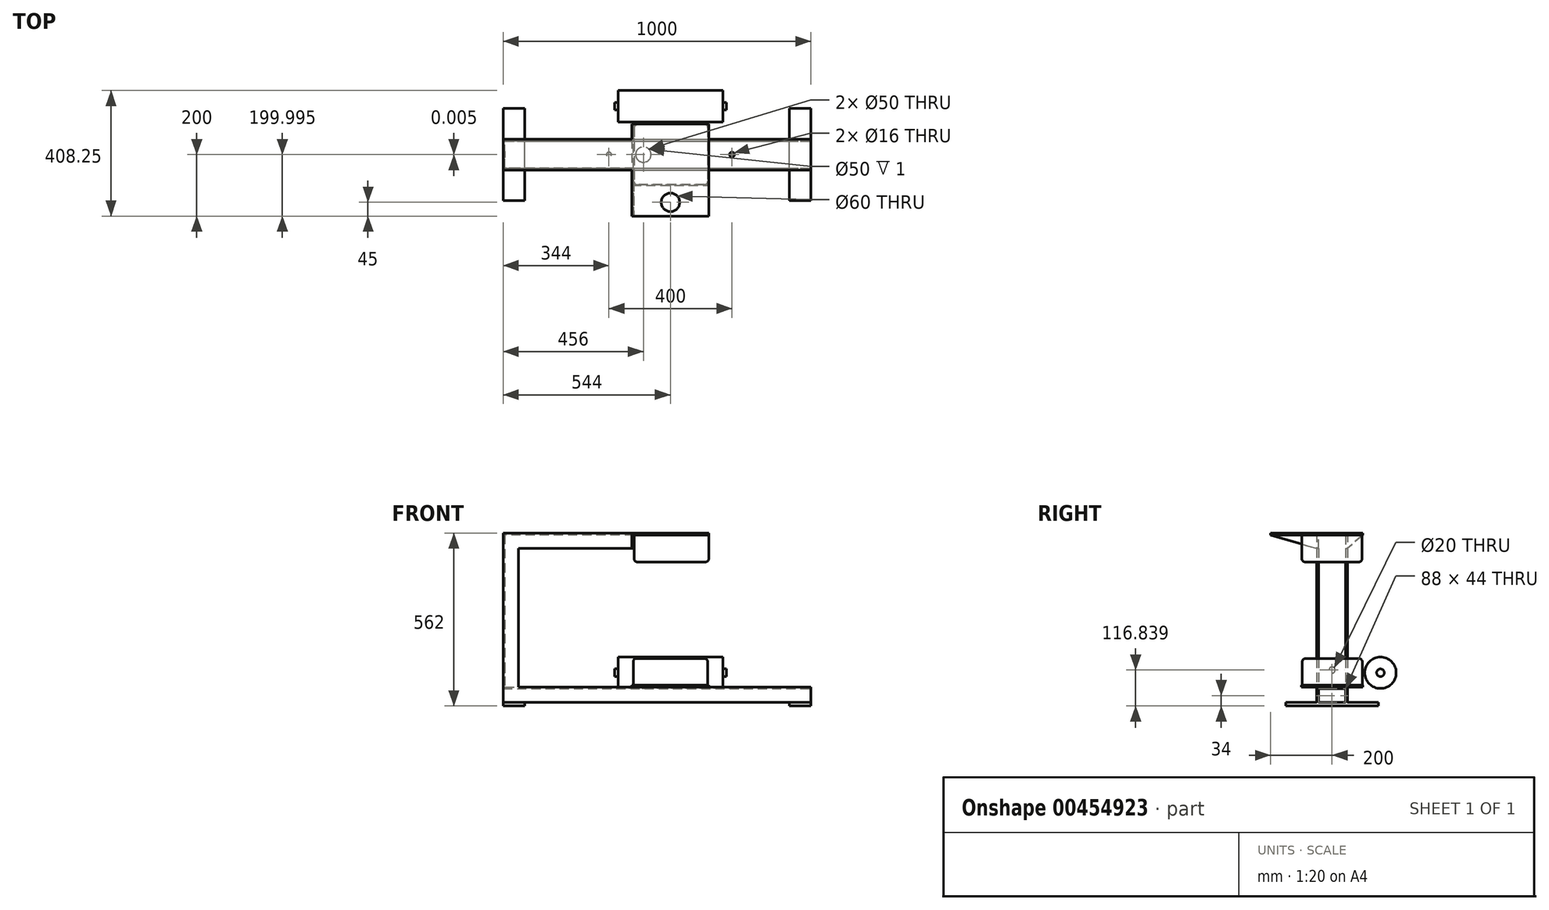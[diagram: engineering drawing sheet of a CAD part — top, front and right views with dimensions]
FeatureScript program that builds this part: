
annotation { "Feature Type Name" : "Feature", "Feature Type Description" : "" }
export const myFeature = defineFeature(function(context is Context, id is Id, definition is map)
    precondition{}
    {
        {
            var Q0;
            Q0=qCreatedBy(makeId("Right.planeOp"),FACE);
            var sketch = newSketch(context, id + "F0", { "sketchPlane" : qUnion([Q0])});
            skLineSegment(sketch, "E0", {"start": v(50, 0) * mm, "end": v(50, 50) * mm});
            skLineSegment(sketch, "E1", {"start": v(50, 50) * mm, "end": v(-50, 50) * mm});
            skLineSegment(sketch, "E2", {"start": v(-50, 50) * mm, "end": v(-50, 0) * mm});
            skLineSegment(sketch, "E3", {"start": v(-50, 0) * mm, "end": v(-44, 0) * mm});
            skLineSegment(sketch, "E4", {"start": v(-44, 0) * mm, "end": v(-44, 44) * mm});
            skLineSegment(sketch, "E5", {"start": v(-44, 44) * mm, "end": v(44, 44) * mm});
            skLineSegment(sketch, "E6", {"start": v(44, 44) * mm, "end": v(44, 0) * mm});
            skLineSegment(sketch, "E7", {"start": v(44, 0) * mm, "end": v(50, 0) * mm});
            skSolve(sketch);
        }
        {
            var Q0;
            Q0=qSketchRegion(id+"F0",true);
            extrude(context, id + "F1", {"entities" : qUnion([Q0]), "oppositeDirection" : true, "depth" : 1000 * mm});
        }
        {
            var Q0;
            Q0=makeQuery(id+"F1.opExtrude","SWEPT_FACE",FACE,{"disambiguationData":[OSD([sQuery(id+"F0.wireOp",EDGE,"E1")])]});
            var sketch = newSketch(context, id + "F2", { "sketchPlane" : qUnion([Q0])});
            skLineSegment(sketch, "E8", {"start": v(-1000, 50) * mm, "end": v(-1000, -50) * mm});
            skLineSegment(sketch, "E9", {"start": v(-1000, -50) * mm, "end": v(-950, -50) * mm});
            skLineSegment(sketch, "E10", {"start": v(-950, -50) * mm, "end": v(-950, -44) * mm});
            skLineSegment(sketch, "E11", {"start": v(-950, -44) * mm, "end": v(-994, -44) * mm});
            skLineSegment(sketch, "E12", {"start": v(-994, -44) * mm, "end": v(-994, 44) * mm});
            skLineSegment(sketch, "E13", {"start": v(-994, 44) * mm, "end": v(-950, 44) * mm});
            skLineSegment(sketch, "E14", {"start": v(-950, 44) * mm, "end": v(-950, 50) * mm});
            skLineSegment(sketch, "E15", {"start": v(-950, 50) * mm, "end": v(-1000, 50) * mm});
            skSolve(sketch);
        }
        {
            var Q0;
            Q0=makeQuery(id+"F2.imprint","IMPRINT",FACE,{"disambiguationData":[TD([[makeQuery(id+"F2.imprint","IMPRINT",EDGE,{"derivedFrom":sQuery(id+"F2.wireOp",EDGE,"E8")}),1.0]])]});
            extrude(context, id + "F3", {"entities" : qUnion([Q0]), "operationType" : NewBodyOperationType.ADD, "depth" : 500 * mm});
        }
        {
            var Q0;
            Q0=makeQuery(id+"F3.opExtrude","SWEPT_FACE",FACE,{"disambiguationData":[OSD([sQuery(id+"F2.wireOp",EDGE,"E14")])]});
            var sketch = newSketch(context, id + "F4", { "sketchPlane" : qUnion([Q0])});
            skLineSegment(sketch, "E16", {"start": v(50, 550) * mm, "end": v(-50, 550) * mm});
            skLineSegment(sketch, "E17", {"start": v(-50, 550) * mm, "end": v(-50, 500) * mm});
            skLineSegment(sketch, "E18", {"start": v(-50, 500) * mm, "end": v(-44, 500) * mm});
            skLineSegment(sketch, "E19", {"start": v(-44, 500) * mm, "end": v(-44, 544) * mm});
            skLineSegment(sketch, "E20", {"start": v(-44, 544) * mm, "end": v(44, 544) * mm});
            skLineSegment(sketch, "E21", {"start": v(44, 544) * mm, "end": v(44, 500) * mm});
            skLineSegment(sketch, "E22", {"start": v(44, 500) * mm, "end": v(50, 500) * mm});
            skLineSegment(sketch, "E23", {"start": v(50, 500) * mm, "end": v(50, 550) * mm});
            skSolve(sketch);
        }
        {
            var Q0;
            Q0=qSketchRegion(id+"F4",true);
            extrude(context, id + "F5", {"entities" : qUnion([Q0]), "operationType" : NewBodyOperationType.ADD, "depth" : 369 * mm, "hasSecondDirection" : true, "secondDirectionOppositeDirection" : true, "secondDirectionDepth" : 50 * mm});
        }
        {
            var Q0;
            Q0=makeQuery(id+"F5.opExtrude","CAP_FACE",FACE,{"disambiguationData":[OSD([sQuery(id+"F4.wireOp",EDGE,"E16"),sQuery(id+"F4.wireOp",EDGE,"E17"),sQuery(id+"F4.wireOp",EDGE,"E18"),sQuery(id+"F4.wireOp",EDGE,"E19"),sQuery(id+"F4.wireOp",EDGE,"E20"),sQuery(id+"F4.wireOp",EDGE,"E21"),sQuery(id+"F4.wireOp",EDGE,"E22"),sQuery(id+"F4.wireOp",EDGE,"E23")])],"isStart":false});
            var sketch = newSketch(context, id + "F6", { "sketchPlane" : qUnion([Q0])});
            skLineSegment(sketch, "E24", {"start": v(0, 550) * mm, "end": v(100, 550) * mm});
            skLineSegment(sketch, "E25", {"start": v(100, 550) * mm, "end": v(100, 544) * mm});
            skLineSegment(sketch, "E26", {"start": v(100, 544) * mm, "end": v(-200, 544) * mm});
            skLineSegment(sketch, "E27", {"start": v(-200, 544) * mm, "end": v(-200, 550) * mm});
            skLineSegment(sketch, "E28", {"start": v(-200, 550) * mm, "end": v(0, 550) * mm});
            skSolve(sketch);
        }
        {
            var Q0;
            Q0=qSketchRegion(id+"F6",true);
            extrude(context, id + "F7", {"entities" : qUnion([Q0]), "operationType" : NewBodyOperationType.ADD, "depth" : 250 * mm});
        }
        {
            var Q0;
            {var subQ0=sQuery(id+"F4.wireOp",EDGE,"E17");var subQ2=sQuery(id+"F4.wireOp",EDGE,"E18");var subQ3=sQuery(id+"F4.wireOp",EDGE,"E19");var subQ4=sQuery(id+"F4.wireOp",EDGE,"E20");Q0=makeQuery(id+"F7.boolean.opBoolean","SPLIT",FACE,{"disambiguationData":[TD([makeQuery(id+"F1.opExtrude","SWEPT_FACE",FACE,{"disambiguationData":[OSD([sQuery(id+"F0.wireOp",EDGE,"E2")])]})])],"derivedFrom":makeQuery(id+"F5.opExtrude","CAP_FACE",FACE,{"disambiguationData":[OSD([sQuery(id+"F4.wireOp",EDGE,"E16"),subQ0,subQ2,subQ3,subQ4,sQuery(id+"F4.wireOp",EDGE,"E21"),sQuery(id+"F4.wireOp",EDGE,"E22"),sQuery(id+"F4.wireOp",EDGE,"E23")])],"isStart":false})});}
            var sketch = newSketch(context, id + "F8", { "sketchPlane" : qUnion([Q0])});
            skLineSegment(sketch, "E29", {"start": v(-44, 544) * mm, "end": v(-200, 544) * mm});
            skLineSegment(sketch, "E30", {"start": v(-200, 544) * mm, "end": v(-50, 500) * mm});
            skLineSegment(sketch, "E31", {"start": v(-50, 500) * mm, "end": v(-44, 500) * mm});
            skLineSegment(sketch, "E32", {"start": v(-44, 544) * mm, "end": v(-44, 500) * mm});
            skSolve(sketch);
        }
        {
            var Q0;
            Q0=qSketchRegion(id+"F8",true);
            extrude(context, id + "F9", {"entities" : qUnion([Q0]), "operationType" : NewBodyOperationType.ADD, "depth" : 6 * mm});
        }
        {
            var Q0;
            {var subQ0=sQuery(id+"F4.wireOp",EDGE,"E20");var subQ2=sQuery(id+"F4.wireOp",EDGE,"E21");var subQ3=sQuery(id+"F4.wireOp",EDGE,"E22");var subQ4=sQuery(id+"F4.wireOp",EDGE,"E23");Q0=makeQuery(id+"F7.boolean.opBoolean","SPLIT",FACE,{"disambiguationData":[TD([makeQuery(id+"F1.opExtrude","SWEPT_FACE",FACE,{"disambiguationData":[OSD([sQuery(id+"F0.wireOp",EDGE,"E0")])]})])],"derivedFrom":makeQuery(id+"F5.opExtrude","CAP_FACE",FACE,{"disambiguationData":[OSD([sQuery(id+"F4.wireOp",EDGE,"E16"),sQuery(id+"F4.wireOp",EDGE,"E17"),sQuery(id+"F4.wireOp",EDGE,"E18"),sQuery(id+"F4.wireOp",EDGE,"E19"),subQ0,subQ2,subQ3,subQ4])],"isStart":false})});}
            var sketch = newSketch(context, id + "F10", { "sketchPlane" : qUnion([Q0])});
            skLineSegment(sketch, "E33", {"start": v(44, 544) * mm, "end": v(100, 544) * mm});
            skLineSegment(sketch, "E34", {"start": v(100, 544) * mm, "end": v(50, 500) * mm});
            skLineSegment(sketch, "E35", {"start": v(50, 500) * mm, "end": v(44, 500) * mm});
            skLineSegment(sketch, "E36", {"start": v(44, 500) * mm, "end": v(44, 544) * mm});
            skSolve(sketch);
        }
        {
            var Q0;
            Q0=qSketchRegion(id+"F10",true);
            extrude(context, id + "F11", {"entities" : qUnion([Q0]), "operationType" : NewBodyOperationType.ADD, "depth" : 6 * mm});
        }
        {
            var Q0;
            Q0=makeQuery(id+"F3.boolean.opBoolean","MERGE",FACE,{"derivedFrom":[makeQuery(id+"F1.opExtrude","CAP_FACE",FACE,{"disambiguationData":[OSD([sQuery(id+"F0.wireOp",EDGE,"E0"),sQuery(id+"F0.wireOp",EDGE,"E1"),sQuery(id+"F0.wireOp",EDGE,"E2"),sQuery(id+"F0.wireOp",EDGE,"E3"),sQuery(id+"F0.wireOp",EDGE,"E4"),sQuery(id+"F0.wireOp",EDGE,"E5"),sQuery(id+"F0.wireOp",EDGE,"E6"),sQuery(id+"F0.wireOp",EDGE,"E7")])],"isStart":false}),makeQuery(id+"F3.opExtrude","SWEPT_FACE",FACE,{"disambiguationData":[OSD([sQuery(id+"F2.wireOp",EDGE,"E8")])]})]});
            var sketch = newSketch(context, id + "F12", { "sketchPlane" : qUnion([Q0])});
            skCircle(sketch, "E37", {"center": v(0, 104.84) * mm, "radius": 10 * mm});
            skSolve(sketch);
        }
        {
            var Q0;
            Q0=makeQuery(id+"F12.imprint","IMPRINT",FACE,{"disambiguationData":[TD([[makeQuery(id+"F12.imprint","IMPRINT",EDGE,{"derivedFrom":sQuery(id+"F12.wireOp",EDGE,"E37")}),1.0]])]});
            extrude(context, id + "F13", {"entities" : qUnion([Q0]), "operationType" : NewBodyOperationType.REMOVE, "endBound" : BoundingType.THROUGH_ALL, "oppositeDirection" : true, "depth" : 25 * mm});
        }
        {
            var Q0;
            Q0=makeQuery(id+"F1.opExtrude","SWEPT_FACE",FACE,{"disambiguationData":[OSD([sQuery(id+"F0.wireOp",EDGE,"E1")])]});
            var sketch = newSketch(context, id + "F14", { "sketchPlane" : qUnion([Q0])});
            skCircle(sketch, "E38", {"center": v(-544, 0) * mm, "radius": 25 * mm});
            skLineSegment(sketch, "E39", {"start": v(-994, 0) * mm, "end": v(-544, 0) * mm});
            skSolve(sketch);
        }
        {
            var Q0;
            Q0=makeQuery(id+"F14.imprint","IMPRINT",FACE,{"disambiguationData":[TD([[makeQuery(id+"F14.imprint","IMPRINT",EDGE,{"derivedFrom":sQuery(id+"F14.wireOp",EDGE,"E38")}),1.0]])]});
            extrude(context, id + "F15", {"entities" : qUnion([Q0]), "operationType" : NewBodyOperationType.REMOVE, "oppositeDirection" : true, "depth" : 6 * mm});
        }
        {
            var Q0;
            Q0=makeQuery(id+"F7.boolean.opBoolean","MERGE",FACE,{"derivedFrom":[makeQuery(id+"F5.boolean.opBoolean","MERGE",FACE,{"derivedFrom":[makeQuery(id+"F3.opExtrude","CAP_FACE",FACE,{"disambiguationData":[OSD([sQuery(id+"F2.wireOp",EDGE,"E8"),sQuery(id+"F2.wireOp",EDGE,"E9"),sQuery(id+"F2.wireOp",EDGE,"E10"),sQuery(id+"F2.wireOp",EDGE,"E11"),sQuery(id+"F2.wireOp",EDGE,"E12"),sQuery(id+"F2.wireOp",EDGE,"E13"),sQuery(id+"F2.wireOp",EDGE,"E14"),sQuery(id+"F2.wireOp",EDGE,"E15")])],"isStart":false}),makeQuery(id+"F5.opExtrude","SWEPT_FACE",FACE,{"disambiguationData":[OSD([sQuery(id+"F4.wireOp",EDGE,"E16")])]})]}),makeQuery(id+"F7.opExtrude","SWEPT_FACE",FACE,{"disambiguationData":[OSD([sQuery(id+"F6.wireOp",EDGE,"E24"),sQuery(id+"F6.wireOp",EDGE,"E28")])]})]});
            var sketch = newSketch(context, id + "F16", { "sketchPlane" : qUnion([Q0])});
            skCircle(sketch, "E40", {"center": v(-456, -155) * mm, "radius": 30 * mm});
            skLineSegment(sketch, "E41", {"start": v(-456, -200) * mm, "end": v(-456, -155) * mm});
            skSolve(sketch);
        }
        {
            var Q0;
            Q0=makeQuery(id+"F16.imprint","IMPRINT",FACE,{"disambiguationData":[TD([[makeQuery(id+"F16.imprint","IMPRINT",EDGE,{"derivedFrom":sQuery(id+"F16.wireOp",EDGE,"E40")}),1.0]])]});
            extrude(context, id + "F17", {"entities" : qUnion([Q0]), "operationType" : NewBodyOperationType.REMOVE, "endBound" : BoundingType.THROUGH_ALL, "oppositeDirection" : true, "depth" : 25 * mm});
        }
        {
            var Q0;
            Q0=makeQuery(id+"F1.opExtrude","SWEPT_FACE",FACE,{"disambiguationData":[OSD([sQuery(id+"F0.wireOp",EDGE,"E1")])]});
            var sketch = newSketch(context, id + "F18", { "sketchPlane" : qUnion([Q0])});
            skLineSegment(sketch, "E42", {"start": v(-556, 100) * mm, "end": v(-556, 50) * mm});
            skLineSegment(sketch, "E43", {"start": v(-331, -100.18) * mm, "end": v(-331, 99.82) * mm});
            skLineSegment(sketch, "E44", {"start": v(-331, 99.82) * mm, "end": v(-581, 99.82) * mm});
            skLineSegment(sketch, "E45", {"start": v(-581, 99.82) * mm, "end": v(-581, -100.18) * mm});
            skLineSegment(sketch, "E46", {"start": v(-581, -100.18) * mm, "end": v(-331, -100.18) * mm});
            skLineSegment(sketch, "E47", {"start": v(-950, -50) * mm, "end": v(-581, -50) * mm});
            skSolve(sketch);
        }
        {
            var Q0;
            Q0=qSketchRegion(id+"F18",true);
            extrude(context, id + "F19", {"entities" : qUnion([Q0]), "operationType" : NewBodyOperationType.ADD, "depth" : 6 * mm});
        }
        {
            var Q0;
            Q0=makeQuery(id+"F1.opExtrude","SWEPT_FACE",FACE,{"disambiguationData":[OSD([sQuery(id+"F0.wireOp",EDGE,"E3")])]});
            var sketch = newSketch(context, id + "F20", { "sketchPlane" : qUnion([Q0])});
            skLineSegment(sketch, "E48", {"start": v(-1000, 50) * mm, "end": v(-1000, 150) * mm});
            skLineSegment(sketch, "E49", {"start": v(-1000, 150) * mm, "end": v(-930, 150) * mm});
            skLineSegment(sketch, "E50", {"start": v(-930, 150) * mm, "end": v(-930, -150) * mm});
            skLineSegment(sketch, "E51", {"start": v(-930, -150) * mm, "end": v(-1000, -150) * mm});
            skLineSegment(sketch, "E52", {"start": v(-1000, -150) * mm, "end": v(-1000, 50) * mm});
            skLineSegment(sketch, "E53", {"start": v(0, 50) * mm, "end": v(0, 150) * mm});
            skLineSegment(sketch, "E54", {"start": v(0, 150) * mm, "end": v(-70, 150) * mm});
            skLineSegment(sketch, "E55", {"start": v(-70, 150) * mm, "end": v(-70, -150) * mm});
            skLineSegment(sketch, "E56", {"start": v(-70, -150) * mm, "end": v(0, -150) * mm});
            skLineSegment(sketch, "E57", {"start": v(0, -150) * mm, "end": v(0, 50) * mm});
            skSolve(sketch);
        }
        {
            var Q0;
            Q0=qSketchRegion(id+"F20",true);
            extrude(context, id + "F21", {"entities" : qUnion([Q0]), "operationType" : NewBodyOperationType.ADD, "depth" : 12 * mm});
        }
        {
            var Q0;
            Q0=makeQuery(id+"F19.boolean.opBoolean","SPLIT",FACE,{"disambiguationData":[TD([makeQuery(id+"F3.opExtrude","SWEPT_FACE",FACE,{"disambiguationData":[OSD([sQuery(id+"F2.wireOp",EDGE,"E10")])]})])],"derivedFrom":makeQuery(id+"F1.opExtrude","SWEPT_FACE",FACE,{"disambiguationData":[OSD([sQuery(id+"F0.wireOp",EDGE,"E1")])]})});
            var sketch = newSketch(context, id + "F22", { "sketchPlane" : qUnion([Q0])});
            skPoint(sketch, "E58.endSnap0", {"position": v(-994, 0) * mm});
            skLineSegment(sketch, "E59", {"start": v(0, 0) * mm, "end": v(-256, 0) * mm});
            skLineSegment(sketch, "E60", {"start": v(-256, 0) * mm, "end": v(-656, 0) * mm});
            skPoint(sketch, "E60.endSnap0", {"position": v(-581, 0) * mm});
            skCircle(sketch, "E61", {"center": v(-656, 0) * mm, "radius": 8 * mm});
            skCircle(sketch, "E62", {"center": v(-256, 0) * mm, "radius": 8 * mm});
            skSolve(sketch);
        }
        {
            var Q0;
            Q0=qSketchRegion(id+"F22",true);
            extrude(context, id + "F23", {"entities" : qUnion([Q0]), "operationType" : NewBodyOperationType.REMOVE, "oppositeDirection" : true, "depth" : 6 * mm});
        }
        {
            var Q0;
            Q0=qCreatedBy(makeId("Top.planeOp"),FACE);
            var sketch = newSketch(context, id + "F24", { "sketchPlane" : qUnion([Q0])});
            skLineSegment(sketch, "E63", {"start": v(93.08, 453.86) * mm, "end": v(288.08, 453.86) * mm});
            skLineSegment(sketch, "E64", {"start": v(288.08, 453.86) * mm, "end": v(288.08, 211.86) * mm});
            skLineSegment(sketch, "E65", {"start": v(288.08, 211.86) * mm, "end": v(93.08, 211.86) * mm});
            skLineSegment(sketch, "E66", {"start": v(93.08, 211.86) * mm, "end": v(93.08, 453.86) * mm});
            skSolve(sketch);
        }
        {
            var Q0;
            Q0=qSketchRegion(id+"F24",true);
            extrude(context, id + "F25", {"entities" : qUnion([Q0]), "depth" : 87 * mm});
        }
        {
            var Q0;
            Q0=makeQuery(id+"F25.opExtrude","CAP_EDGE",EDGE,{"disambiguationData":[OSD([sQuery(id+"F24.wireOp",EDGE,"E64")])],"isStart":false});
            var Q1;
            Q1=makeQuery(id+"F25.opExtrude","CAP_EDGE",EDGE,{"disambiguationData":[OSD([sQuery(id+"F24.wireOp",EDGE,"E66")])],"isStart":false});
            var Q2;
            Q2=makeQuery(id+"F25.opExtrude","CAP_EDGE",EDGE,{"disambiguationData":[OSD([sQuery(id+"F24.wireOp",EDGE,"E65")])],"isStart":false});
            var Q3;
            Q3=makeQuery(id+"F25.opExtrude","CAP_EDGE",EDGE,{"disambiguationData":[OSD([sQuery(id+"F24.wireOp",EDGE,"E63")])],"isStart":false});
            var Q4;
            Q4=makeQuery(id+"F25.opExtrude","SWEPT_EDGE",EDGE,{"disambiguationData":[OSD([sQuery(id+"F24.wireOp",EDGE,"E63"),sQuery(id+"F24.wireOp",EDGE,"E64")])]});
            var Q5;
            Q5=makeQuery(id+"F25.opExtrude","SWEPT_EDGE",EDGE,{"disambiguationData":[OSD([sQuery(id+"F24.wireOp",EDGE,"E64"),sQuery(id+"F24.wireOp",EDGE,"E65")])]});
            var Q6;
            Q6=makeQuery(id+"F25.opExtrude","SWEPT_EDGE",EDGE,{"disambiguationData":[OSD([sQuery(id+"F24.wireOp",EDGE,"E65"),sQuery(id+"F24.wireOp",EDGE,"E66")])]});
            var Q7;
            Q7=makeQuery(id+"F25.opExtrude","SWEPT_EDGE",EDGE,{"disambiguationData":[OSD([sQuery(id+"F24.wireOp",EDGE,"E63"),sQuery(id+"F24.wireOp",EDGE,"E66")])]});
            fillet(context, id + "F26", {"entities" : qUnion([Q0, Q1, Q2, Q3, Q4, Q5, Q6, Q7]), "radius" : 10 * mm, "tangentPropagation" : true, "allowEdgeOverflow" : false});
        }
        {
            var Q0;
            Q0=makeQuery(id+"F25.opExtrude","SWEPT_BODY",BODY,{"disambiguationData":[OSD([sQuery(id+"F24.wireOp",EDGE,"E63"),sQuery(id+"F24.wireOp",EDGE,"E64"),sQuery(id+"F24.wireOp",EDGE,"E65"),sQuery(id+"F24.wireOp",EDGE,"E66")])]});
            transform(context, id + "F27", {"entities" : qUnion([Q0]), "transformType" : TransformType.TRANSLATION_3D, "dx" : -646 * mm, "dy" : -333 * mm, "dz" : 55 * mm, "makeCopy" : true});
        }
        {
            var Q0;
            Q0=makeQuery(id+"F25.opExtrude","SWEPT_BODY",BODY,{"disambiguationData":[OSD([sQuery(id+"F24.wireOp",EDGE,"E63"),sQuery(id+"F24.wireOp",EDGE,"E64"),sQuery(id+"F24.wireOp",EDGE,"E65"),sQuery(id+"F24.wireOp",EDGE,"E66")])]});
            transform(context, id + "F28", {"entities" : qUnion([Q0]), "transformType" : TransformType.TRANSLATION_3D, "dx" : -454 * mm, "dy" : 0 * mm, "dz" : 418 * mm, "makeCopy" : false});
        }
        {
            var Q0;
            Q0=makeQuery(id+"F25.opExtrude","SWEPT_BODY",BODY,{"disambiguationData":[OSD([sQuery(id+"F24.wireOp",EDGE,"E63"),sQuery(id+"F24.wireOp",EDGE,"E64"),sQuery(id+"F24.wireOp",EDGE,"E65"),sQuery(id+"F24.wireOp",EDGE,"E66")])]});
            var Q1;
            Q1=makeQuery(id+"F25.opExtrude","CAP_EDGE",EDGE,{"disambiguationData":[OSD([sQuery(id+"F24.wireOp",EDGE,"E65")])],"isStart":true});
            transform(context, id + "F29", {"entities" : qUnion([Q0]), "transformType" : TransformType.ROTATION, "transformAxis" : qUnion([Q1]), "angle" : 180 * degree, "makeCopy" : false});
        }
        {
            var Q0;
            Q0=makeQuery(id+"F25.opExtrude","SWEPT_BODY",BODY,{"disambiguationData":[OSD([sQuery(id+"F24.wireOp",EDGE,"E63"),sQuery(id+"F24.wireOp",EDGE,"E64"),sQuery(id+"F24.wireOp",EDGE,"E65"),sQuery(id+"F24.wireOp",EDGE,"E66")])]});
            transform(context, id + "F30", {"entities" : qUnion([Q0]), "transformType" : TransformType.TRANSLATION_3D, "dx" : -193 * mm, "dy" : -92 * mm, "dz" : 125 * mm, "makeCopy" : false});
        }
        {
            var Q0;
            Q0=qCreatedBy(makeId("Right.planeOp"),FACE);
            cPlane(context, id + "F31", {"entities" : qUnion([Q0]), "cplaneType" : CPlaneType.OFFSET, "offset" : 456 * mm, "oppositeDirection" : true, "width" : 150 * mm, "height" : 150 * mm});
        }
        {
            var Q0;
            Q0=qCreatedBy(id+"F31.planeOp",FACE);
            var sketch = newSketch(context, id + "F32", { "sketchPlane" : qUnion([Q0])});
            skLineSegment(sketch, "E67", {"start": v(0, -106.93) * mm, "end": v(0, 589) * mm, "construction": true});
            skSolve(sketch);
        }
        {
            var Q0;
            Q0=makeQuery(id+"F25.opExtrude","SWEPT_BODY",BODY,{"disambiguationData":[OSD([sQuery(id+"F24.wireOp",EDGE,"E63"),sQuery(id+"F24.wireOp",EDGE,"E64"),sQuery(id+"F24.wireOp",EDGE,"E65"),sQuery(id+"F24.wireOp",EDGE,"E66")])]});
            var Q1;
            Q1=sQuery(id+"F32.wireOp",EDGE,"E67");
            transform(context, id + "F33", {"entities" : qUnion([Q0]), "transformType" : TransformType.ROTATION, "transformAxis" : qUnion([Q1]), "angle" : 90 * degree, "makeCopy" : false});
        }
        {
            var Q0;
            Q0=makeQuery(id+"F27.opPattern","COPY",BODY,{"derivedFrom":makeQuery(id+"F25.opExtrude","SWEPT_BODY",BODY,{"disambiguationData":[OSD([sQuery(id+"F24.wireOp",EDGE,"E63"),sQuery(id+"F24.wireOp",EDGE,"E64"),sQuery(id+"F24.wireOp",EDGE,"E65"),sQuery(id+"F24.wireOp",EDGE,"E66")])]}),"instanceName":"1"});
            var Q1;
            Q1=sQuery(id+"F32.wireOp",EDGE,"E67");
            transform(context, id + "F34", {"entities" : qUnion([Q0]), "transformType" : TransformType.ROTATION, "transformAxis" : qUnion([Q1]), "angle" : 90 * degree, "makeCopy" : false});
        }
        {
            var Q0;
            Q0=makeQuery(id+"F25.opExtrude","SWEPT_BODY",BODY,{"disambiguationData":[OSD([sQuery(id+"F24.wireOp",EDGE,"E63"),sQuery(id+"F24.wireOp",EDGE,"E64"),sQuery(id+"F24.wireOp",EDGE,"E65"),sQuery(id+"F24.wireOp",EDGE,"E66")])]});
            transform(context, id + "F35", {"entities" : qUnion([Q0]), "transformType" : TransformType.TRANSLATION_3D, "dx" : 2 * mm, "dy" : 0 * mm, "dz" : 0 * mm, "makeCopy" : false});
        }
        {
            var Q0;
            {var subQ0=sQuery(id+"F18.wireOp",EDGE,"E43");var subQ1=sQuery(id+"F18.wireOp",EDGE,"E45");var subQ2=sQuery(id+"F18.wireOp",EDGE,"E46");Q0=makeQuery(id+"F19.boolean.opBoolean","SPLIT",FACE,{"disambiguationData":[TD([makeQuery(id+"F1.opExtrude","SWEPT_FACE",FACE,{"disambiguationData":[OSD([sQuery(id+"F0.wireOp",EDGE,"E2")])]})])],"derivedFrom":makeQuery(id+"F19.opExtrude","CAP_FACE",FACE,{"disambiguationData":[OSD([subQ0,sQuery(id+"F18.wireOp",EDGE,"E44"),subQ1,subQ2])],"isStart":true})});}
            var sketch = newSketch(context, id + "F36", { "sketchPlane" : qUnion([Q0])});
            skLineSegment(sketch, "E68", {"start": v(0, 0) * mm, "end": v(-11.87, 0) * mm});
            skCircle(sketch, "E69", {"center": v(-544, 0) * mm, "radius": 25 * mm});
            skLineSegment(sketch, "E70", {"start": v(0, 0) * mm, "end": v(-544, 0) * mm});
            skSolve(sketch);
        }
        {
            var Q0;
            Q0=qSketchRegion(id+"F36",true);
            extrude(context, id + "F37", {"entities" : qUnion([Q0]), "operationType" : NewBodyOperationType.REMOVE, "oppositeDirection" : true, "depth" : 6 * mm});
        }
        {
            var Q0;
            Q0=qCreatedBy(makeId("Right.planeOp"),FACE);
            var sketch = newSketch(context, id + "F38", { "sketchPlane" : qUnion([Q0])});
            skCircle(sketch, "E71", {"center": v(213.25, 96.1) * mm, "radius": 51 * mm});
            skSolve(sketch);
        }
        {
            var Q0;
            Q0=makeQuery(id+"F38.imprint","IMPRINT",FACE,{"disambiguationData":[TD([[makeQuery(id+"F38.imprint","IMPRINT",EDGE,{"derivedFrom":sQuery(id+"F38.wireOp",EDGE,"E71")}),1.0]])]});
            extrude(context, id + "F39", {"entities" : qUnion([Q0]), "depth" : 340 * mm});
        }
        {
            var Q0;
            Q0=makeQuery(id+"F39.opExtrude","CAP_FACE",FACE,{"disambiguationData":[OSD([sQuery(id+"F38.wireOp",EDGE,"E71")])],"isStart":false});
            var sketch = newSketch(context, id + "F40", { "sketchPlane" : qUnion([Q0])});
            skCircle(sketch, "E72", {"center": v(213.25, 96.1) * mm, "radius": 12.5 * mm});
            skSolve(sketch);
        }
        {
            var Q0;
            Q0=makeQuery(id+"F40.imprint","IMPRINT",FACE,{"disambiguationData":[TD([[makeQuery(id+"F40.imprint","IMPRINT",EDGE,{"derivedFrom":sQuery(id+"F40.wireOp",EDGE,"E72")}),1.0]])]});
            extrude(context, id + "F41", {"entities" : qUnion([Q0]), "operationType" : NewBodyOperationType.ADD, "depth" : 12 * mm});
        }
        {
            var Q0;
            Q0=makeQuery(id+"F39.opExtrude","CAP_FACE",FACE,{"disambiguationData":[OSD([sQuery(id+"F38.wireOp",EDGE,"E71")])],"isStart":true});
            var sketch = newSketch(context, id + "F42", { "sketchPlane" : qUnion([Q0])});
            skCircle(sketch, "E73", {"center": v(-213.25, 96.1) * mm, "radius": 12.5 * mm});
            skSolve(sketch);
        }
        {
            var Q0;
            Q0=makeQuery(id+"F42.imprint","IMPRINT",FACE,{"disambiguationData":[TD([[makeQuery(id+"F42.imprint","IMPRINT",EDGE,{"derivedFrom":sQuery(id+"F42.wireOp",EDGE,"E73")}),1.0]])]});
            extrude(context, id + "F43", {"entities" : qUnion([Q0]), "operationType" : NewBodyOperationType.ADD, "depth" : 12 * mm});
        }
        {
            var Q0;
            Q0=makeQuery(id+"F39.opExtrude","SWEPT_BODY",BODY,{"disambiguationData":[OSD([sQuery(id+"F38.wireOp",EDGE,"E71")])]});
            transform(context, id + "F44", {"entities" : qUnion([Q0]), "transformType" : TransformType.TRANSLATION_3D, "dx" : -625 * mm, "dy" : -56 * mm, "dz" : 0 * mm, "makeCopy" : false});
        }
        {
            var Q0;
            Q0=makeQuery(id+"F39.opExtrude","SWEPT_BODY",BODY,{"disambiguationData":[OSD([sQuery(id+"F38.wireOp",EDGE,"E71")])]});
            transform(context, id + "F45", {"entities" : qUnion([Q0]), "transformType" : TransformType.TRANSLATION_3D, "dx" : -1 * mm, "dy" : 0 * mm, "dz" : 0 * mm, "makeCopy" : false});
        }
    });
